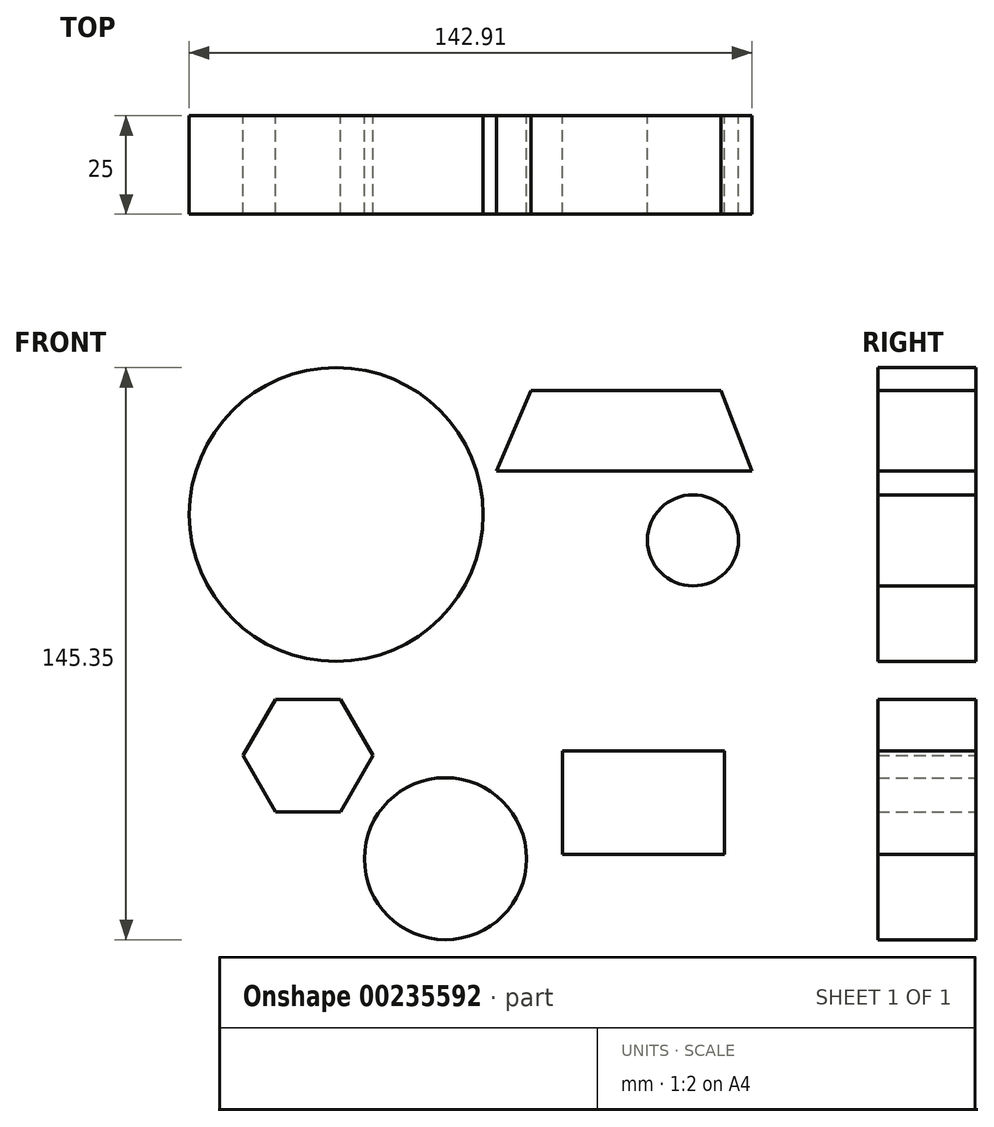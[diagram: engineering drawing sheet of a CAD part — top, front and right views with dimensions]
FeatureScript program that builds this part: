
annotation { "Feature Type Name" : "Feature", "Feature Type Description" : "" }
export const myFeature = defineFeature(function(context is Context, id is Id, definition is map)
    precondition{}
    {
        {
            var Q0;
            Q0=qCreatedBy(makeId("Front.planeOp"),FACE);
            var sketch = newSketch(context, id + "F0", { "sketchPlane" : qUnion([Q0])});
            skLineSegment(sketch, "E0", {"start": v(2.75, 47.54) * mm, "end": v(11.54, 67.93) * mm});
            skLineSegment(sketch, "E1", {"start": v(11.54, 67.93) * mm, "end": v(59.8, 67.93) * mm});
            skCircle(sketch, "E2", {"center": v(-37.98, 36.47) * mm, "radius": 37.32 * mm});
            skPoint(sketch, "E3.0.midPoint", {"position": v(27.81, -74.51) * mm});
            skLineSegment(sketch, "E4", {"start": v(2.75, 47.54) * mm, "end": v(67.6, 47.54) * mm});
            skLineSegment(sketch, "E5", {"start": v(59.8, 67.93) * mm, "end": v(67.6, 47.54) * mm});
            skLineSegment(sketch, "E6.bottom", {"start": v(19.44, -23.62) * mm, "end": v(60.71, -23.62) * mm});
            skLineSegment(sketch, "E6.top", {"start": v(19.44, -49.83) * mm, "end": v(60.71, -49.83) * mm});
            skLineSegment(sketch, "E6.left", {"start": v(19.44, -23.62) * mm, "end": v(19.44, -49.83) * mm});
            skLineSegment(sketch, "E6.right", {"start": v(60.71, -23.62) * mm, "end": v(60.71, -49.83) * mm});
            skCircle(sketch, "E7.cCircle", {"center": v(-45.17, -24.77) * mm, "radius": 14.3 * mm, "construction": true});
            skLineSegment(sketch, "E7.0", {"start": v(-36.91, -39.07) * mm, "end": v(-53.42, -39.07) * mm});
            skLineSegment(sketch, "E7.1", {"start": v(-53.42, -39.07) * mm, "end": v(-61.68, -24.77) * mm});
            skLineSegment(sketch, "E7.2", {"start": v(-61.68, -24.77) * mm, "end": v(-53.42, -10.47) * mm});
            skLineSegment(sketch, "E7.3", {"start": v(-53.42, -10.47) * mm, "end": v(-36.91, -10.47) * mm});
            skLineSegment(sketch, "E7.4", {"start": v(-36.91, -10.47) * mm, "end": v(-28.66, -24.77) * mm});
            skLineSegment(sketch, "E7.5", {"start": v(-28.66, -24.77) * mm, "end": v(-36.91, -39.07) * mm});
            skPoint(sketch, "E7.0.midPoint", {"position": v(-45.17, -39.07) * mm});
            skCircle(sketch, "E8", {"center": v(52.66, 29.91) * mm, "radius": 11.58 * mm});
            skCircle(sketch, "E9", {"center": v(-10.24, -50.97) * mm, "radius": 20.59 * mm});
            skSolve(sketch);
        }
        {
            var Q0;
            Q0=makeQuery(id+"F0.imprint","IMPRINT",FACE,{"disambiguationData":[TD([[makeQuery(id+"F0.imprint","IMPRINT",EDGE,{"derivedFrom":sQuery(id+"F0.wireOp",EDGE,"E8")}),1.0]])]});
            var Q1;
            Q1=makeQuery(id+"F0.imprint","IMPRINT",FACE,{"disambiguationData":[TD([[makeQuery(id+"F0.imprint","IMPRINT",EDGE,{"derivedFrom":sQuery(id+"F0.wireOp",EDGE,"E0")}),-1.0]])]});
            var Q2;
            Q2=makeQuery(id+"F0.imprint","IMPRINT",FACE,{"disambiguationData":[TD([[makeQuery(id+"F0.imprint","IMPRINT",EDGE,{"derivedFrom":sQuery(id+"F0.wireOp",EDGE,"E6.bottom")}),-1.0]])]});
            var Q3;
            Q3=makeQuery(id+"F0.imprint","IMPRINT",FACE,{"disambiguationData":[TD([[makeQuery(id+"F0.imprint","IMPRINT",EDGE,{"derivedFrom":sQuery(id+"F0.wireOp",EDGE,"E9")}),1.0]])]});
            var Q4;
            Q4=makeQuery(id+"F0.imprint","IMPRINT",FACE,{"disambiguationData":[TD([[makeQuery(id+"F0.imprint","IMPRINT",EDGE,{"derivedFrom":sQuery(id+"F0.wireOp",EDGE,"E7.0")}),-1.0]])]});
            extrude(context, id + "F1", {"entities" : qUnion([Q0, Q1, Q2, Q3, Q4]), "depth" : 25 * mm});
        }
        {
            var Q0;
            Q0=makeQuery(id+"F0.imprint","IMPRINT",FACE,{"disambiguationData":[TD([[makeQuery(id+"F0.imprint","IMPRINT",EDGE,{"derivedFrom":sQuery(id+"F0.wireOp",EDGE,"E2")}),1.0]])]});
            extrude(context, id + "F2", {"entities" : qUnion([Q0]), "depth" : 25 * mm});
        }
    });
